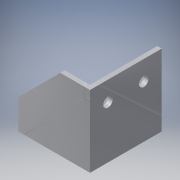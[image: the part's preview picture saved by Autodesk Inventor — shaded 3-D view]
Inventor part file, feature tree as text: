
AUTODESK INVENTOR PART (.ipt)
format: ipt  version: 2016 (Build 200138000, 138)  size: 135,168 bytes
history: native  units: in
note: dims shown in document units (in); Inventor stores cm internally (conversion verified against a paired STEP export)
features: extrude x4, sketch x4
ambient origin geometry x8: Origin, YZ Plane, XZ Plane, XY Plane, X Axis, Y Axis, Z Axis, Center Point
bodies: Solid1 (feature_tree)
feature tree (8):
  extrude  "Extrusion1"  Depth=2.0in
  extrude  "Extrusion2"  TaperAngle=135.0deg  [1 undecoded]
  extrude  "Extrusion3"  Depth=0.125in
  extrude  "Extrusion5"  Depth=0.125in
  sketch  "Sketch1"  dims[d0=2.0in d2=2.0in]
  sketch  "Sketch2"  dims[d3=2.0in d4=135.0deg]
  sketch  "Sketch3"  dims[d5=0.125in d6=0.0in d7=0.125in]
  sketch  "Sketch5"  dims[d8=2.0in d9=0.0in d10=0.2656in d11=0.2656in d14=0.5in d15=1.0in d16=0.125in d17=0.0in d25=0.547in d26=0.547in d27=0.2656in d28=0.2656in d29=0.5in d30=0.5in d31=1.0in d32=1.0in d33=0.5in d34=0.125in d35=0.0in]
note: 1 required parameter value undecoded (feature->parameter linkage not recoverable at this tier; creation-order binding heuristic only, values carry confidence <= 0.55)
